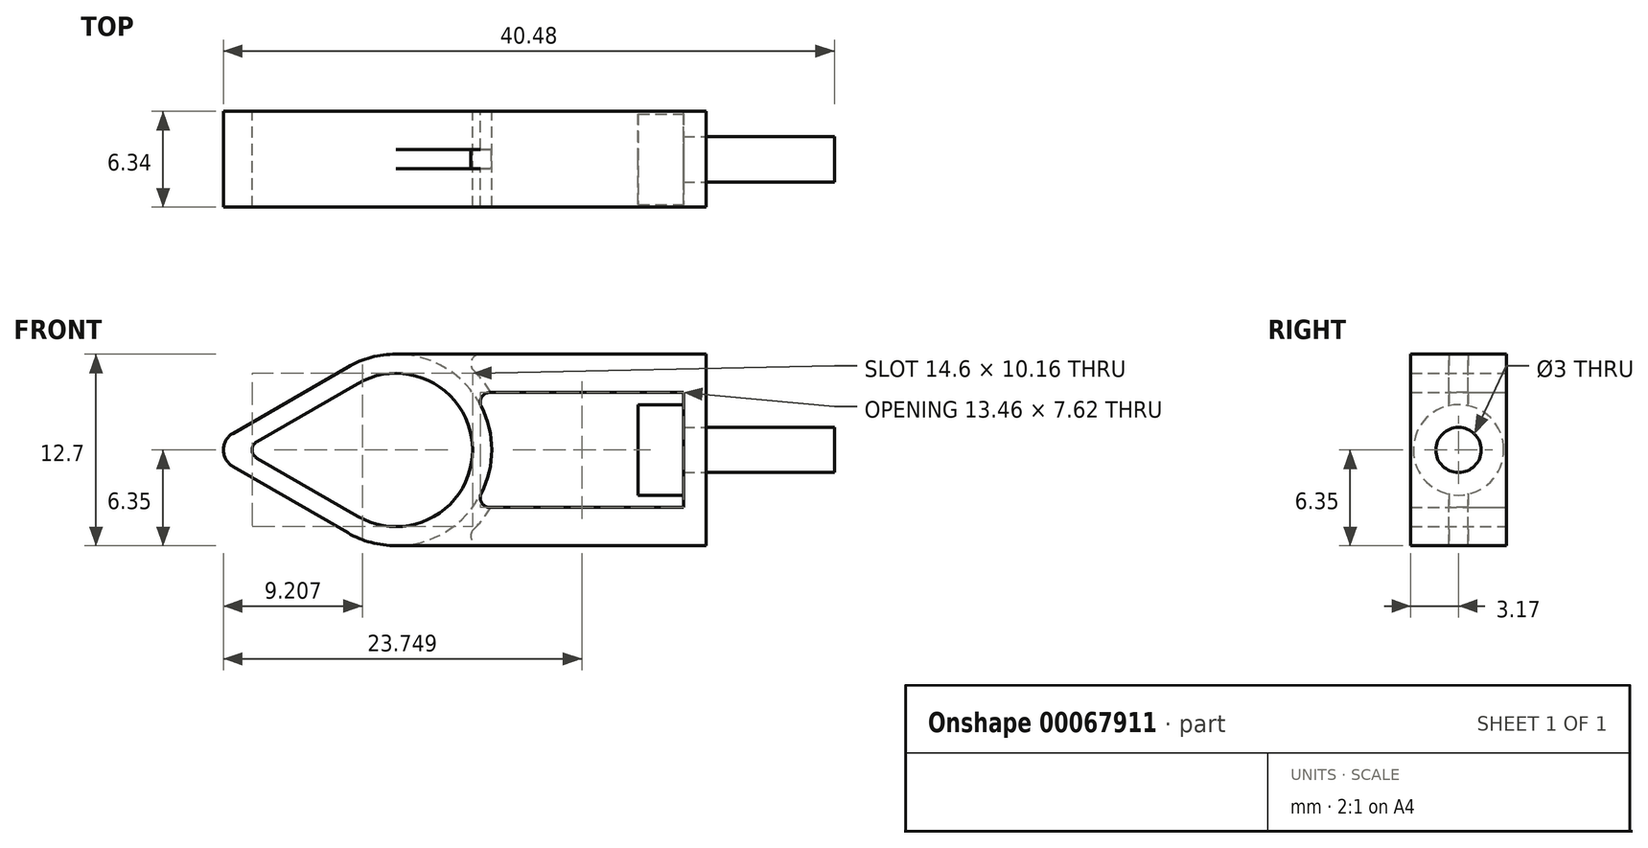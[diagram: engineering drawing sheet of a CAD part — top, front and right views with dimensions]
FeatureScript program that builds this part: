
annotation { "Feature Type Name" : "Feature", "Feature Type Description" : "" }
export const myFeature = defineFeature(function(context is Context, id is Id, definition is map)
    precondition{}
    {
        {
            var Q0;
            Q0=qCreatedBy(makeId("Front.planeOp"),FACE);
            var sketch = newSketch(context, id + "F0", { "sketchPlane" : qUnion([Q0])});
            skLineSegment(sketch, "E0", {"start": v(-3, 0) * mm, "end": v(-3, 3) * mm});
            skLineSegment(sketch, "E1", {"start": v(-3, 3) * mm, "end": v(0, 3) * mm});
            skLineSegment(sketch, "E2", {"start": v(0, 3) * mm, "end": v(0, 1.5) * mm});
            skLineSegment(sketch, "E3", {"start": v(0, 1.5) * mm, "end": v(10, 1.5) * mm});
            skLineSegment(sketch, "E4", {"start": v(10, 1.5) * mm, "end": v(10, 0) * mm});
            skLineSegment(sketch, "E5", {"start": v(10, 0) * mm, "end": v(-3, 0) * mm});
            skSolve(sketch);
        }
        {
            var Q0;
            Q0=makeQuery(id+"F0.imprint","IMPRINT",FACE,{"disambiguationData":[TD([[makeQuery(id+"F0.imprint","IMPRINT",EDGE,{"derivedFrom":sQuery(id+"F0.wireOp",EDGE,"E0")}),-1.0]])]});
            var Q1;
            Q1=sQuery(id+"F0.wireOp",EDGE,"E5");
            revolve(context, id + "F1", {"entities" : qUnion([Q0]), "axis" : qUnion([Q1]), "revolveType" : RevolveType.FULL});
        }
        {
            var Q0;
            Q0=qCreatedBy(makeId("Front.planeOp"),FACE);
            var sketch = newSketch(context, id + "F2", { "sketchPlane" : qUnion([Q0])});
            skArc(sketch, "E6", {"start": v(-13.4, -2.89) * mm, "mid": v(-12.7, 0) * mm, "end": v(-13.4, 2.89) * mm});
            skLineSegment(sketch, "E7", {"start": v(-22.23, 5.5) * mm, "end": v(-29.85, 1.1) * mm});
            skLineSegment(sketch, "E8", {"start": v(-19.05, 6.35) * mm, "end": v(1.5, 6.35) * mm});
            skLineSegment(sketch, "E9", {"start": v(1.5, 0) * mm, "end": v(1.5, 6.35) * mm});
            skLineSegment(sketch, "E10.MirrorCS", {"start": v(1.5, 0) * mm, "end": v(1.5, -6.35) * mm});
            skLineSegment(sketch, "E11.MirrorCS", {"start": v(-22.22, -5.5) * mm, "end": v(-29.85, -1.1) * mm});
            skLineSegment(sketch, "E12.MirrorCS", {"start": v(-19.05, -6.35) * mm, "end": v(1.5, -6.35) * mm});
            skArc(sketch, "E13.MirrorCS", {"start": v(-19.05, -6.35) * mm, "mid": v(-20.7, -6.13) * mm, "end": v(-22.22, -5.5) * mm});
            skLineSegment(sketch, "E14.top", {"start": v(0, -3.8) * mm, "end": v(-12.83, -3.81) * mm});
            skLineSegment(sketch, "E14.left", {"start": v(0, 3.81) * mm, "end": v(0, -3.8) * mm});
            skLineSegment(sketch, "E15", {"start": v(0, 3.81) * mm, "end": v(-12.83, 3.81) * mm});
            skPoint(sketch, "E16.visualSharp", {"position": v(-16.97, 3.81) * mm});
            skPoint(sketch, "E17.visualSharp", {"position": v(-16.97, -3.81) * mm});
            skPoint(sketch, "E18.visualSharp", {"position": v(-31.75, 0) * mm});
            skArc(sketch, "E18.filletArc", {"start": v(-29.85, 1.1) * mm, "mid": v(-30.48, 0) * mm, "end": v(-29.85, -1.1) * mm});
            skLineSegment(sketch, "E19.0", {"start": v(-21.59, -4.4) * mm, "end": v(-28.26, -0.55) * mm});
            skLineSegment(sketch, "E19.1", {"start": v(-21.59, 4.4) * mm, "end": v(-28.26, 0.55) * mm});
            skPoint(sketch, "E20.visualSharp", {"position": v(-29.2, 0) * mm});
            skArc(sketch, "E20.filletArc", {"start": v(-28.26, 0.55) * mm, "mid": v(-28.58, 0) * mm, "end": v(-28.26, -0.55) * mm});
            skArc(sketch, "E21.trimOffspring", {"start": v(-19.05, 6.35) * mm, "mid": v(-20.7, 6.13) * mm, "end": v(-22.23, 5.5) * mm});
            skArc(sketch, "E22", {"start": v(-21.59, -4.4) * mm, "mid": v(-13.97, 0) * mm, "end": v(-21.59, 4.4) * mm});
            skPoint(sketch, "E23.visualSharp", {"position": v(-13.97, 3.81) * mm});
            skArc(sketch, "E23.filletArc", {"start": v(-12.83, 3.81) * mm, "mid": v(-13.37, 3.5) * mm, "end": v(-13.4, 2.89) * mm});
            skPoint(sketch, "E24.visualSharp", {"position": v(-13.97, -3.81) * mm});
            skArc(sketch, "E24.filletArc", {"start": v(-13.4, -2.89) * mm, "mid": v(-13.37, -3.5) * mm, "end": v(-12.83, -3.81) * mm});
            skSolve(sketch);
        }
        {
            var Q0;
            Q0=makeQuery(id+"F2.imprint","IMPRINT",FACE,{"disambiguationData":[TD([[makeQuery(id+"F2.imprint","IMPRINT",EDGE,{"derivedFrom":sQuery(id+"F2.wireOp",EDGE,"E6")}),1.0]])]});
            extrude(context, id + "F3", {"entities" : qUnion([Q0]), "endBound" : BoundingType.SYMMETRIC, "depth" : 6.35 * mm});
        }
        {
            var Q0;
            Q0=qCreatedBy(makeId("Front.planeOp"),FACE);
            var sketch = newSketch(context, id + "F4", { "sketchPlane" : qUnion([Q0])});
            skArc(sketch, "E25.converted", {"start": v(-19.05, -6.35) * mm, "mid": v(-12.7, 0) * mm, "end": v(-19.05, 6.35) * mm});
            skPoint(sketch, "E26.orphan", {"position": v(-13.4, 2.89) * mm});
            skArc(sketch, "E27.0", {"start": v(-19.05, -7.37) * mm, "mid": v(-11.68, 0) * mm, "end": v(-19.05, 7.37) * mm});
            skLineSegment(sketch, "E28", {"start": v(-19.05, 7.37) * mm, "end": v(-19.05, 6.35) * mm});
            skPoint(sketch, "E29.orphan", {"position": v(-19.05, 8.97) * mm});
            skLineSegment(sketch, "E30.trimOffspring", {"start": v(-19.05, -6.35) * mm, "end": v(-19.05, -7.37) * mm});
            skSolve(sketch);
        }
        {
            var Q0;
            Q0=makeQuery(id+"F4.imprint","IMPRINT",FACE,{"disambiguationData":[TD([[makeQuery(id+"F4.imprint","IMPRINT",EDGE,{"derivedFrom":sQuery(id+"F4.wireOp",EDGE,"E25.converted")}),-1.0]])]});
            extrude(context, id + "F5", {"entities" : qUnion([Q0]), "operationType" : NewBodyOperationType.REMOVE, "endBound" : BoundingType.SYMMETRIC, "oppositeDirection" : true, "depth" : 1.27 * mm});
        }
        {
            var Q0;
            Q0=makeQuery(id+"F5.boolean.opBoolean","INTERSECT",EDGE,{"derivedFrom":[makeQuery(id+"F3.opExtrude","SWEPT_FACE",FACE,{"disambiguationData":[OSD([sQuery(id+"F2.wireOp",EDGE,"E8")])]}),makeQuery(id+"F5.opExtrude","SWEPT_FACE",FACE,{"disambiguationData":[OSD([sQuery(id+"F4.wireOp",EDGE,"E27.0")])]})]});
            var Q1;
            Q1=makeQuery(id+"F5.boolean.opBoolean","INTERSECT",EDGE,{"derivedFrom":[makeQuery(id+"F3.opExtrude","SWEPT_FACE",FACE,{"disambiguationData":[OSD([sQuery(id+"F2.wireOp",EDGE,"E12.MirrorCS")])]}),makeQuery(id+"F5.opExtrude","SWEPT_FACE",FACE,{"disambiguationData":[OSD([sQuery(id+"F4.wireOp",EDGE,"E27.0")])]})]});
            fillet(context, id + "F6", {"entities" : qUnion([Q0, Q1]), "radius" : 0.64 * mm, "tangentPropagation" : true, "allowEdgeOverflow" : false});
        }
        {
            var Q0;
            Q0=makeQuery(id+"F3.opExtrude","SWEPT_FACE",FACE,{"disambiguationData":[OSD([sQuery(id+"F2.wireOp",EDGE,"E9"),sQuery(id+"F2.wireOp",EDGE,"E10.MirrorCS")])]});
            var sketch = newSketch(context, id + "F7", { "sketchPlane" : qUnion([Q0])});
            skPoint(sketch, "E31", {"position": v(0, 0) * mm});
            skSolve(sketch);
        }
        {
            var Q0;
            Q0=sQuery(id+"F7.wireOp",VERTEX,"E31");
            var Q1;
            Q1=makeQuery(id+"F3.opExtrude","SWEPT_BODY",BODY,{"disambiguationData":[OSD([sQuery(id+"F2.wireOp",EDGE,"E6"),sQuery(id+"F2.wireOp",EDGE,"E7"),sQuery(id+"F2.wireOp",EDGE,"E8"),sQuery(id+"F2.wireOp",EDGE,"E9"),sQuery(id+"F2.wireOp",EDGE,"E10.MirrorCS"),sQuery(id+"F2.wireOp",EDGE,"E11.MirrorCS"),sQuery(id+"F2.wireOp",EDGE,"E12.MirrorCS"),sQuery(id+"F2.wireOp",EDGE,"E13.MirrorCS"),sQuery(id+"F2.wireOp",EDGE,"E14.top"),sQuery(id+"F2.wireOp",EDGE,"E14.left"),sQuery(id+"F2.wireOp",EDGE,"E15"),sQuery(id+"F2.wireOp",EDGE,"E18.filletArc"),sQuery(id+"F2.wireOp",EDGE,"E19.0"),sQuery(id+"F2.wireOp",EDGE,"E19.1"),sQuery(id+"F2.wireOp",EDGE,"E20.filletArc"),sQuery(id+"F2.wireOp",EDGE,"E21.trimOffspring"),sQuery(id+"F2.wireOp",EDGE,"E22"),sQuery(id+"F2.wireOp",EDGE,"E23.filletArc"),sQuery(id+"F2.wireOp",EDGE,"E24.filletArc")])]});
            hole(context, id + "F8", {"style" : HoleStyle.SIMPLE, "endStyle" : HoleEndStyle.BLIND, "holeDiameter" : 3 * mm, "holeDepth" : 12.7 * mm, "locations" : qUnion([Q0]), "scope" : qUnion([Q1])});
        }
    });
